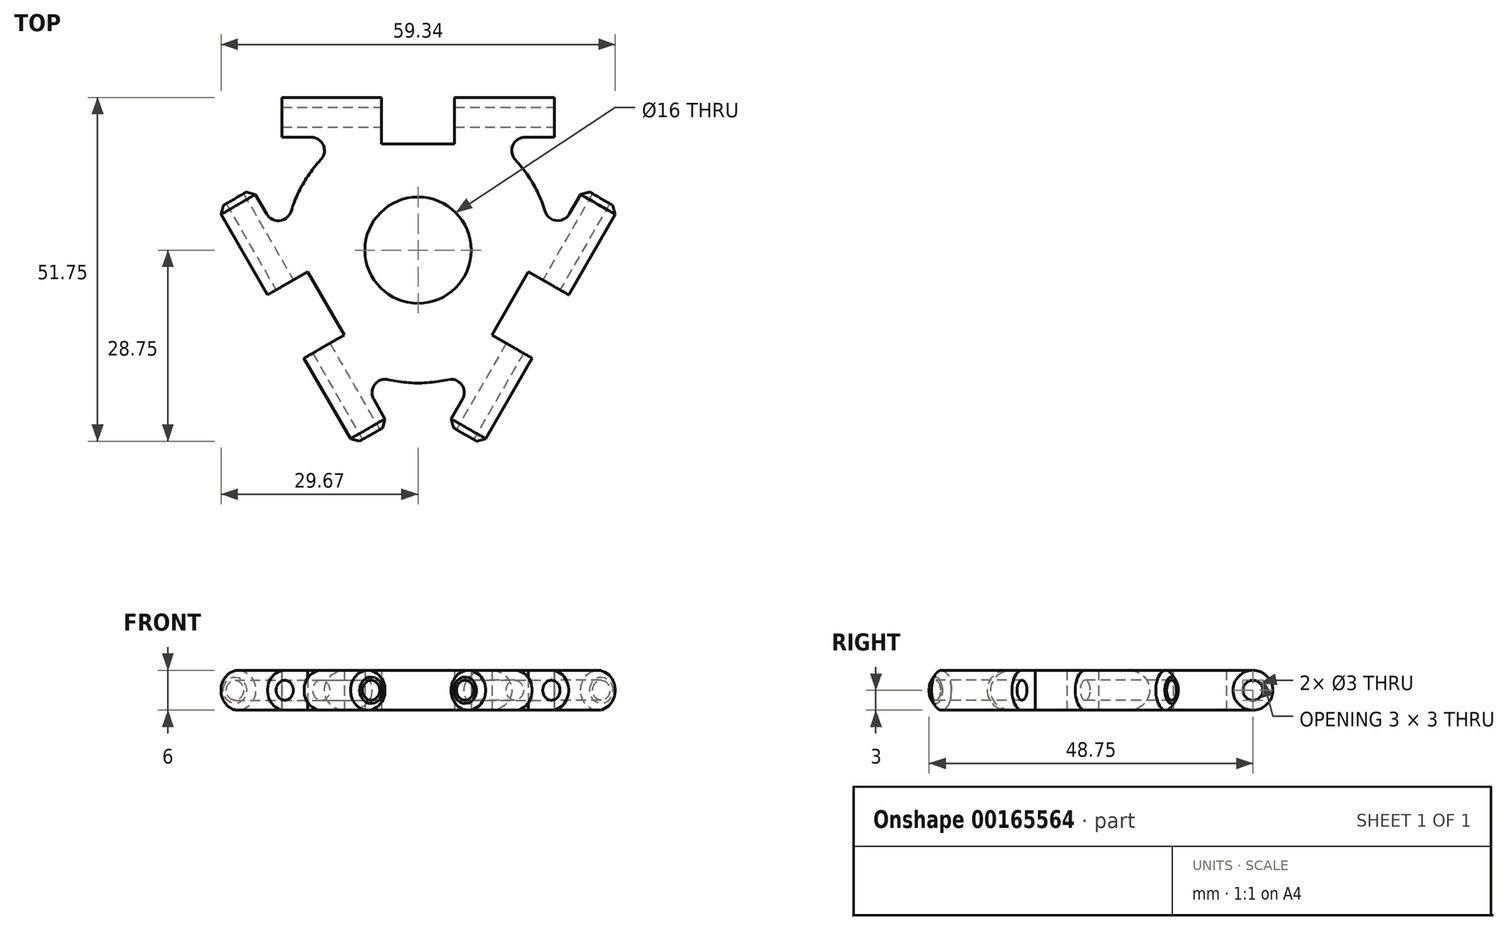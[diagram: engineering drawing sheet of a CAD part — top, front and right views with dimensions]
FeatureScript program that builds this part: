
annotation { "Feature Type Name" : "Feature", "Feature Type Description" : "" }
export const myFeature = defineFeature(function(context is Context, id is Id, definition is map)
    precondition{}
    {
        {
            var Q0;
            Q0=qCreatedBy(makeId("Top.planeOp"),FACE);
            var sketch = newSketch(context, id + "F0", { "sketchPlane" : qUnion([Q0])});
            skCircle(sketch, "E0", {"center": v(0, 0) * mm, "radius": 8 * mm});
            skArc(sketch, "E1", {"start": v(-14.63, 13.64) * mm, "mid": v(-17.32, 10) * mm, "end": v(-19.12, 5.85) * mm});
            skLineSegment(sketch, "E2.bottom", {"start": v(-20.5, 23) * mm, "end": v(20.5, 23) * mm});
            skLineSegment(sketch, "E2.top", {"start": v(-20.5, 17) * mm, "end": v(-16.1, 17) * mm});
            skLineSegment(sketch, "E2.left", {"start": v(-20.5, 23) * mm, "end": v(-20.5, 17) * mm});
            skLineSegment(sketch, "E2.right", {"start": v(20.5, 23) * mm, "end": v(20.5, 17) * mm});
            skLineSegment(sketch, "E3.trimOffspring", {"start": v(16.1, 17) * mm, "end": v(20.5, 17) * mm});
            skPoint(sketch, "E4.visualSharp", {"position": v(-10.54, 17) * mm});
            skArc(sketch, "E4.filletArc", {"start": v(-14.63, 13.64) * mm, "mid": v(-14.26, 15.8) * mm, "end": v(-16.1, 17) * mm});
            skPoint(sketch, "E5.visualSharp", {"position": v(10.54, 17) * mm});
            skArc(sketch, "E5.filletArc", {"start": v(16.1, 17) * mm, "mid": v(14.26, 15.8) * mm, "end": v(14.63, 13.64) * mm});
            skLineSegment(sketch, "E6.bottom", {"start": v(-30.17, 6.25) * mm, "end": v(-24.97, 9.25) * mm});
            skLineSegment(sketch, "E6.top", {"start": v(-9.67, -29.25) * mm, "end": v(-4.47, -26.25) * mm});
            skLineSegment(sketch, "E6.left", {"start": v(-30.17, 6.25) * mm, "end": v(-9.67, -29.25) * mm});
            skLineSegment(sketch, "E6.right", {"start": v(-24.97, 9.25) * mm, "end": v(-22.77, 5.44) * mm});
            skLineSegment(sketch, "E7", {"start": v(0, 0) * mm, "end": v(-28.49, -16.45) * mm, "construction": true});
            skLineSegment(sketch, "E8.trimOffspring", {"start": v(-6.68, -22.44) * mm, "end": v(-4.47, -26.25) * mm});
            skArc(sketch, "E9.trimOffspring", {"start": v(-4.5, -19.49) * mm, "mid": v(0, -20) * mm, "end": v(4.5, -19.49) * mm});
            skPoint(sketch, "E10.firstSnap0", {"position": v(-22.48, 4.94) * mm});
            skLineSegment(sketch, "E11.bottom", {"start": v(24.97, 9.25) * mm, "end": v(30.17, 6.25) * mm});
            skLineSegment(sketch, "E11.top", {"start": v(4.47, -26.25) * mm, "end": v(9.67, -29.25) * mm});
            skLineSegment(sketch, "E11.left", {"start": v(24.97, 9.25) * mm, "end": v(22.77, 5.44) * mm});
            skLineSegment(sketch, "E11.right", {"start": v(30.17, 6.25) * mm, "end": v(9.67, -29.25) * mm});
            skLineSegment(sketch, "E12", {"start": v(0, 0) * mm, "end": v(25.77, -14.88) * mm, "construction": true});
            skLineSegment(sketch, "E13.trimOffspring", {"start": v(6.68, -22.44) * mm, "end": v(4.47, -26.25) * mm});
            skArc(sketch, "E14.trimOffspring", {"start": v(19.12, 5.85) * mm, "mid": v(17.32, 10) * mm, "end": v(14.63, 13.64) * mm});
            skPoint(sketch, "E15.visualSharp", {"position": v(-20, 0.62) * mm});
            skArc(sketch, "E15.filletArc", {"start": v(-22.77, 5.44) * mm, "mid": v(-20.81, 4.45) * mm, "end": v(-19.12, 5.85) * mm});
            skPoint(sketch, "E16.visualSharp", {"position": v(-9.45, -17.62) * mm});
            skArc(sketch, "E16.filletArc", {"start": v(-4.5, -19.49) * mm, "mid": v(-6.55, -20.25) * mm, "end": v(-6.68, -22.44) * mm});
            skPoint(sketch, "E17.visualSharp", {"position": v(9.45, -17.62) * mm});
            skArc(sketch, "E17.filletArc", {"start": v(6.68, -22.44) * mm, "mid": v(6.55, -20.25) * mm, "end": v(4.5, -19.49) * mm});
            skPoint(sketch, "E18.visualSharp", {"position": v(20, 0.62) * mm});
            skArc(sketch, "E18.filletArc", {"start": v(19.12, 5.85) * mm, "mid": v(20.81, 4.45) * mm, "end": v(22.77, 5.44) * mm});
            skSolve(sketch);
        }
        {
            var Q0;
            Q0=makeQuery(id+"F0.imprint","IMPRINT",FACE,{"disambiguationData":[TD([[makeQuery(id+"F0.imprint","IMPRINT",EDGE,{"derivedFrom":sQuery(id+"F0.wireOp",EDGE,"E0")}),-1.0]])]});
            extrude(context, id + "F1", {"entities" : qUnion([Q0]), "depth" : 6 * mm});
        }
        {
            var Q0;
            Q0=makeQuery(id+"F1.opExtrude","SWEPT_FACE",FACE,{"disambiguationData":[OSD([sQuery(id+"F0.wireOp",EDGE,"E6.top")])]});
            var sketch = newSketch(context, id + "F2", { "sketchPlane" : qUnion([Q0])});
            skLineSegment(sketch, "E19", {"start": v(-23, 6) * mm, "end": v(-17, 0) * mm, "construction": true});
            skCircle(sketch, "E20", {"center": v(-20, 3) * mm, "radius": 1.5 * mm});
            skSolve(sketch);
        }
        {
            var Q0;
            Q0=makeQuery(id+"F2.imprint","IMPRINT",FACE,{"disambiguationData":[TD([[makeQuery(id+"F2.imprint","IMPRINT",EDGE,{"derivedFrom":sQuery(id+"F2.wireOp",EDGE,"E20")}),1.0]])]});
            extrude(context, id + "F3", {"entities" : qUnion([Q0]), "operationType" : NewBodyOperationType.REMOVE, "endBound" : BoundingType.THROUGH_ALL, "oppositeDirection" : true, "depth" : 25 * mm});
        }
        {
            var Q0;
            Q0=makeQuery(id+"F1.opExtrude","SWEPT_FACE",FACE,{"disambiguationData":[OSD([sQuery(id+"F0.wireOp",EDGE,"E11.top")])]});
            var sketch = newSketch(context, id + "F4", { "sketchPlane" : qUnion([Q0])});
            skLineSegment(sketch, "E21", {"start": v(17, 0) * mm, "end": v(23, 6) * mm, "construction": true});
            skCircle(sketch, "E22", {"center": v(20, 3) * mm, "radius": 1.5 * mm});
            skSolve(sketch);
        }
        {
            var Q0;
            Q0=makeQuery(id+"F4.imprint","IMPRINT",FACE,{"disambiguationData":[TD([[makeQuery(id+"F4.imprint","IMPRINT",EDGE,{"derivedFrom":sQuery(id+"F4.wireOp",EDGE,"E22")}),1.0]])]});
            var Q1;
            Q1=sQuery(id+"F4.wireOp",EDGE,"E22");
            extrude(context, id + "F5", {"entities" : qUnion([Q0]), "operationType" : NewBodyOperationType.REMOVE, "surfaceEntities" : qUnion([Q1]), "endBound" : BoundingType.THROUGH_ALL, "oppositeDirection" : true, "depth" : 25 * mm});
        }
        {
            var Q0;
            Q0=makeQuery(id+"F1.opExtrude","CAP_EDGE",EDGE,{"disambiguationData":[OSD([sQuery(id+"F0.wireOp",EDGE,"E11.right")])],"isStart":false});
            fillet(context, id + "F6", {"entities" : qUnion([Q0]), "radius" : 3 * mm, "tangentPropagation" : true, "allowEdgeOverflow" : false});
        }
        {
            var Q0;
            Q0=makeQuery(id+"F1.opExtrude","CAP_EDGE",EDGE,{"disambiguationData":[OSD([sQuery(id+"F0.wireOp",EDGE,"E11.right")])],"isStart":true});
            fillet(context, id + "F7", {"entities" : qUnion([Q0]), "radius" : 3 * mm, "tangentPropagation" : true, "allowEdgeOverflow" : false});
        }
        {
            var Q0;
            Q0=makeQuery(id+"F1.opExtrude","CAP_EDGE",EDGE,{"disambiguationData":[OSD([sQuery(id+"F0.wireOp",EDGE,"E13.trimOffspring")])],"isStart":false});
            var Q1;
            Q1=makeQuery(id+"F1.opExtrude","CAP_EDGE",EDGE,{"disambiguationData":[OSD([sQuery(id+"F0.wireOp",EDGE,"E13.trimOffspring")])],"isStart":true});
            fillet(context, id + "F8", {"entities" : qUnion([Q0, Q1]), "radius" : 3 * mm, "tangentPropagation" : true, "allowEdgeOverflow" : false});
        }
        {
            var Q0;
            Q0=makeQuery(id+"F6.opFillet","BLEND_EDGE",EDGE,{"blendedFrom":[makeQuery(id+"F1.opExtrude","CAP_EDGE",EDGE,{"disambiguationData":[OSD([sQuery(id+"F0.wireOp",EDGE,"E11.right")])],"isStart":false}),makeQuery(id+"F1.opExtrude","SWEPT_FACE",FACE,{"disambiguationData":[OSD([sQuery(id+"F0.wireOp",EDGE,"E11.top")])]})],"blendedInto":[makeQuery(id+"F1.opExtrude","SWEPT_FACE",FACE,{"disambiguationData":[OSD([sQuery(id+"F0.wireOp",EDGE,"E11.top")])]})]});
            chamfer(context, id + "F9", {"entities" : qUnion([Q0]), "width" : 1 * mm, "tangentPropagation" : true});
        }
        {
            var Q0;
            Q0=makeQuery(id+"F1.opExtrude","CAP_EDGE",EDGE,{"disambiguationData":[OSD([sQuery(id+"F0.wireOp",EDGE,"E6.left")])],"isStart":false});
            var Q1;
            Q1=makeQuery(id+"F1.opExtrude","CAP_EDGE",EDGE,{"disambiguationData":[OSD([sQuery(id+"F0.wireOp",EDGE,"E6.left")])],"isStart":true});
            fillet(context, id + "F10", {"entities" : qUnion([Q0, Q1]), "radius" : 3 * mm, "tangentPropagation" : true, "allowEdgeOverflow" : false});
        }
        {
            var Q0;
            Q0=makeQuery(id+"F10.opFillet","BLEND_EDGE",EDGE,{"blendedFrom":[makeQuery(id+"F1.opExtrude","CAP_EDGE",EDGE,{"disambiguationData":[OSD([sQuery(id+"F0.wireOp",EDGE,"E6.left")])],"isStart":false}),makeQuery(id+"F1.opExtrude","SWEPT_FACE",FACE,{"disambiguationData":[OSD([sQuery(id+"F0.wireOp",EDGE,"E6.top")])]})],"blendedInto":[makeQuery(id+"F1.opExtrude","SWEPT_FACE",FACE,{"disambiguationData":[OSD([sQuery(id+"F0.wireOp",EDGE,"E6.top")])]})]});
            chamfer(context, id + "F11", {"entities" : qUnion([Q0]), "width" : 1 * mm, "tangentPropagation" : true});
        }
        {
            var Q0;
            Q0=makeQuery(id+"F1.opExtrude","SWEPT_FACE",FACE,{"disambiguationData":[OSD([sQuery(id+"F0.wireOp",EDGE,"E2.right")])]});
            var sketch = newSketch(context, id + "F12", { "sketchPlane" : qUnion([Q0])});
            skLineSegment(sketch, "E23", {"start": v(23, 6) * mm, "end": v(17, 0) * mm, "construction": true});
            skCircle(sketch, "E24", {"center": v(20, 3) * mm, "radius": 1.5 * mm});
            skSolve(sketch);
        }
        {
            var Q0;
            Q0=makeQuery(id+"F12.imprint","IMPRINT",FACE,{"disambiguationData":[TD([[makeQuery(id+"F12.imprint","IMPRINT",EDGE,{"derivedFrom":sQuery(id+"F12.wireOp",EDGE,"E24")}),1.0]])]});
            extrude(context, id + "F13", {"entities" : qUnion([Q0]), "operationType" : NewBodyOperationType.REMOVE, "endBound" : BoundingType.THROUGH_ALL, "oppositeDirection" : true, "depth" : 25 * mm});
        }
        {
            var Q0;
            Q0=makeQuery(id+"F1.opExtrude","CAP_EDGE",EDGE,{"disambiguationData":[OSD([sQuery(id+"F0.wireOp",EDGE,"E2.bottom")])],"isStart":true});
            var Q1;
            Q1=makeQuery(id+"F1.opExtrude","CAP_EDGE",EDGE,{"disambiguationData":[OSD([sQuery(id+"F0.wireOp",EDGE,"E2.bottom")])],"isStart":false});
            var Q2;
            Q2=makeQuery(id+"F1.opExtrude","CAP_EDGE",EDGE,{"disambiguationData":[OSD([sQuery(id+"F0.wireOp",EDGE,"E3.trimOffspring")])],"isStart":false});
            var Q3;
            Q3=makeQuery(id+"F1.opExtrude","CAP_EDGE",EDGE,{"disambiguationData":[OSD([sQuery(id+"F0.wireOp",EDGE,"E2.top")])],"isStart":false});
            var Q4;
            Q4=makeQuery(id+"F1.opExtrude","CAP_EDGE",EDGE,{"disambiguationData":[OSD([sQuery(id+"F0.wireOp",EDGE,"E3.trimOffspring")])],"isStart":true});
            var Q5;
            Q5=makeQuery(id+"F1.opExtrude","CAP_EDGE",EDGE,{"disambiguationData":[OSD([sQuery(id+"F0.wireOp",EDGE,"E2.top")])],"isStart":true});
            fillet(context, id + "F14", {"entities" : qUnion([Q0, Q1, Q2, Q3, Q4, Q5]), "radius" : 3 * mm, "tangentPropagation" : true, "allowEdgeOverflow" : false});
        }
        {
            var Q0;
            Q0=makeQuery(id+"F14.opFillet","BLEND_EDGE",EDGE,{"blendedFrom":[makeQuery(id+"F1.opExtrude","CAP_EDGE",EDGE,{"disambiguationData":[OSD([sQuery(id+"F0.wireOp",EDGE,"E11.left")])],"isStart":false}),makeQuery(id+"F1.opExtrude","SWEPT_FACE",FACE,{"disambiguationData":[OSD([sQuery(id+"F0.wireOp",EDGE,"E11.bottom")])]})],"blendedInto":[makeQuery(id+"F1.opExtrude","SWEPT_FACE",FACE,{"disambiguationData":[OSD([sQuery(id+"F0.wireOp",EDGE,"E11.bottom")])]})]});
            var Q1;
            Q1=makeQuery(id+"F14.opFillet","BLEND_EDGE",EDGE,{"blendedFrom":[makeQuery(id+"F1.opExtrude","CAP_EDGE",EDGE,{"disambiguationData":[OSD([sQuery(id+"F0.wireOp",EDGE,"E3.trimOffspring")])],"isStart":false}),makeQuery(id+"F1.opExtrude","SWEPT_FACE",FACE,{"disambiguationData":[OSD([sQuery(id+"F0.wireOp",EDGE,"E2.right")])]})],"blendedInto":[makeQuery(id+"F1.opExtrude","SWEPT_FACE",FACE,{"disambiguationData":[OSD([sQuery(id+"F0.wireOp",EDGE,"E2.right")])]})]});
            var Q2;
            Q2=makeQuery(id+"F14.opFillet","BLEND_EDGE",EDGE,{"blendedFrom":[makeQuery(id+"F1.opExtrude","CAP_EDGE",EDGE,{"disambiguationData":[OSD([sQuery(id+"F0.wireOp",EDGE,"E2.top")])],"isStart":false}),makeQuery(id+"F1.opExtrude","SWEPT_FACE",FACE,{"disambiguationData":[OSD([sQuery(id+"F0.wireOp",EDGE,"E2.left")])]})],"blendedInto":[makeQuery(id+"F1.opExtrude","SWEPT_FACE",FACE,{"disambiguationData":[OSD([sQuery(id+"F0.wireOp",EDGE,"E2.left")])]})]});
            var Q3;
            Q3=makeQuery(id+"F10.opFillet","BLEND_EDGE",EDGE,{"blendedFrom":[makeQuery(id+"F1.opExtrude","CAP_EDGE",EDGE,{"disambiguationData":[OSD([sQuery(id+"F0.wireOp",EDGE,"E6.left")])],"isStart":false}),makeQuery(id+"F1.opExtrude","SWEPT_FACE",FACE,{"disambiguationData":[OSD([sQuery(id+"F0.wireOp",EDGE,"E6.bottom")])]})],"blendedInto":[makeQuery(id+"F1.opExtrude","SWEPT_FACE",FACE,{"disambiguationData":[OSD([sQuery(id+"F0.wireOp",EDGE,"E6.bottom")])]})]});
            chamfer(context, id + "F15", {"entities" : qUnion([Q0, Q1, Q2, Q3]), "width" : 1 * mm, "tangentPropagation" : true});
        }
        {
            var Q0;
            Q0=makeQuery(id+"F1.opExtrude","CAP_FACE",FACE,{"disambiguationData":[OSD([sQuery(id+"F0.wireOp",EDGE,"E0"),sQuery(id+"F0.wireOp",EDGE,"E1"),sQuery(id+"F0.wireOp",EDGE,"E2.bottom"),sQuery(id+"F0.wireOp",EDGE,"E2.top"),sQuery(id+"F0.wireOp",EDGE,"E2.left"),sQuery(id+"F0.wireOp",EDGE,"E2.right"),sQuery(id+"F0.wireOp",EDGE,"E3.trimOffspring"),sQuery(id+"F0.wireOp",EDGE,"E4.filletArc"),sQuery(id+"F0.wireOp",EDGE,"E5.filletArc"),sQuery(id+"F0.wireOp",EDGE,"E6.bottom"),sQuery(id+"F0.wireOp",EDGE,"E6.top"),sQuery(id+"F0.wireOp",EDGE,"E6.left"),sQuery(id+"F0.wireOp",EDGE,"E6.right"),sQuery(id+"F0.wireOp",EDGE,"E8.trimOffspring"),sQuery(id+"F0.wireOp",EDGE,"E9.trimOffspring"),sQuery(id+"F0.wireOp",EDGE,"E11.bottom"),sQuery(id+"F0.wireOp",EDGE,"E11.top"),sQuery(id+"F0.wireOp",EDGE,"E11.left"),sQuery(id+"F0.wireOp",EDGE,"E11.right"),sQuery(id+"F0.wireOp",EDGE,"E13.trimOffspring"),sQuery(id+"F0.wireOp",EDGE,"E14.trimOffspring"),sQuery(id+"F0.wireOp",EDGE,"E15.filletArc"),sQuery(id+"F0.wireOp",EDGE,"E16.filletArc"),sQuery(id+"F0.wireOp",EDGE,"E17.filletArc"),sQuery(id+"F0.wireOp",EDGE,"E18.filletArc")])],"isStart":true});
            var sketch = newSketch(context, id + "F16", { "sketchPlane" : qUnion([Q0])});
            skLineSegment(sketch, "E25.bottom", {"start": v(11.1, 12.76) * mm, "end": v(20.57, 18.23) * mm});
            skLineSegment(sketch, "E25.top", {"start": v(16.6, 3.24) * mm, "end": v(26.07, 8.7) * mm});
            skLineSegment(sketch, "E25.left", {"start": v(11.1, 12.76) * mm, "end": v(16.6, 3.24) * mm});
            skLineSegment(sketch, "E25.right", {"start": v(20.57, 18.23) * mm, "end": v(26.07, 8.7) * mm});
            skLineSegment(sketch, "E26", {"start": v(0, 0) * mm, "end": v(22.36, 12.91) * mm, "construction": true});
            skLineSegment(sketch, "E27.1.0", {"start": v(-11.1, 12.76) * mm, "end": v(-20.57, 18.23) * mm});
            skLineSegment(sketch, "E27.1.1", {"start": v(-26.07, 8.7) * mm, "end": v(-20.57, 18.23) * mm});
            skLineSegment(sketch, "E27.1.2", {"start": v(-16.6, 3.24) * mm, "end": v(-11.1, 12.76) * mm});
            skLineSegment(sketch, "E27.1.3", {"start": v(-16.6, 3.24) * mm, "end": v(-26.07, 8.7) * mm});
            skLineSegment(sketch, "E27.2.0", {"start": v(-5.5, -16) * mm, "end": v(-5.5, -26.93) * mm});
            skLineSegment(sketch, "E27.2.1", {"start": v(5.5, -26.93) * mm, "end": v(-5.5, -26.93) * mm});
            skLineSegment(sketch, "E27.2.2", {"start": v(5.5, -16) * mm, "end": v(-5.5, -16) * mm});
            skLineSegment(sketch, "E27.2.3", {"start": v(5.5, -16) * mm, "end": v(5.5, -26.93) * mm});
            skPoint(sketch, "E27.center", {"position": v(0, 0) * mm});
            skSolve(sketch);
        }
        {
            var Q0;
            {var subQ0=sQuery(id+"F16.wireOp",EDGE,"E27.1.1");Q0=makeQuery(id+"F16.imprint","IMPRINT",FACE,{"disambiguationData":[TD([[makeQuery(id+"F16.imprint","IMPRINT",EDGE,{"derivedFrom":subQ0}),-1.0]])]});}
            var Q1;
            {var subQ0=sQuery(id+"F16.wireOp",EDGE,"E27.1.2");Q1=makeQuery(id+"F16.imprint","IMPRINT",FACE,{"disambiguationData":[TD([[makeQuery(id+"F16.imprint","IMPRINT",EDGE,{"derivedFrom":subQ0}),1.0]])]});}
            var Q2;
            {var subQ0=sQuery(id+"F16.wireOp",EDGE,"E25.left");Q2=makeQuery(id+"F16.imprint","IMPRINT",FACE,{"disambiguationData":[TD([[makeQuery(id+"F16.imprint","IMPRINT",EDGE,{"derivedFrom":subQ0}),1.0]])]});}
            var Q3;
            {var subQ0=sQuery(id+"F16.wireOp",EDGE,"E25.right");Q3=makeQuery(id+"F16.imprint","IMPRINT",FACE,{"disambiguationData":[TD([[makeQuery(id+"F16.imprint","IMPRINT",EDGE,{"derivedFrom":subQ0}),-1.0]])]});}
            var Q4;
            {var subQ0=sQuery(id+"F16.wireOp",EDGE,"E27.2.2");Q4=makeQuery(id+"F16.imprint","IMPRINT",FACE,{"disambiguationData":[TD([[makeQuery(id+"F16.imprint","IMPRINT",EDGE,{"derivedFrom":subQ0}),1.0]])]});}
            var Q5;
            {var subQ0=sQuery(id+"F16.wireOp",EDGE,"E27.2.1");Q5=makeQuery(id+"F16.imprint","IMPRINT",FACE,{"disambiguationData":[TD([[makeQuery(id+"F16.imprint","IMPRINT",EDGE,{"derivedFrom":subQ0}),-1.0]])]});}
            extrude(context, id + "F17", {"entities" : qUnion([Q0, Q1, Q2, Q3, Q4, Q5]), "operationType" : NewBodyOperationType.REMOVE, "endBound" : BoundingType.THROUGH_ALL, "oppositeDirection" : true, "depth" : 25 * mm});
        }
    });
